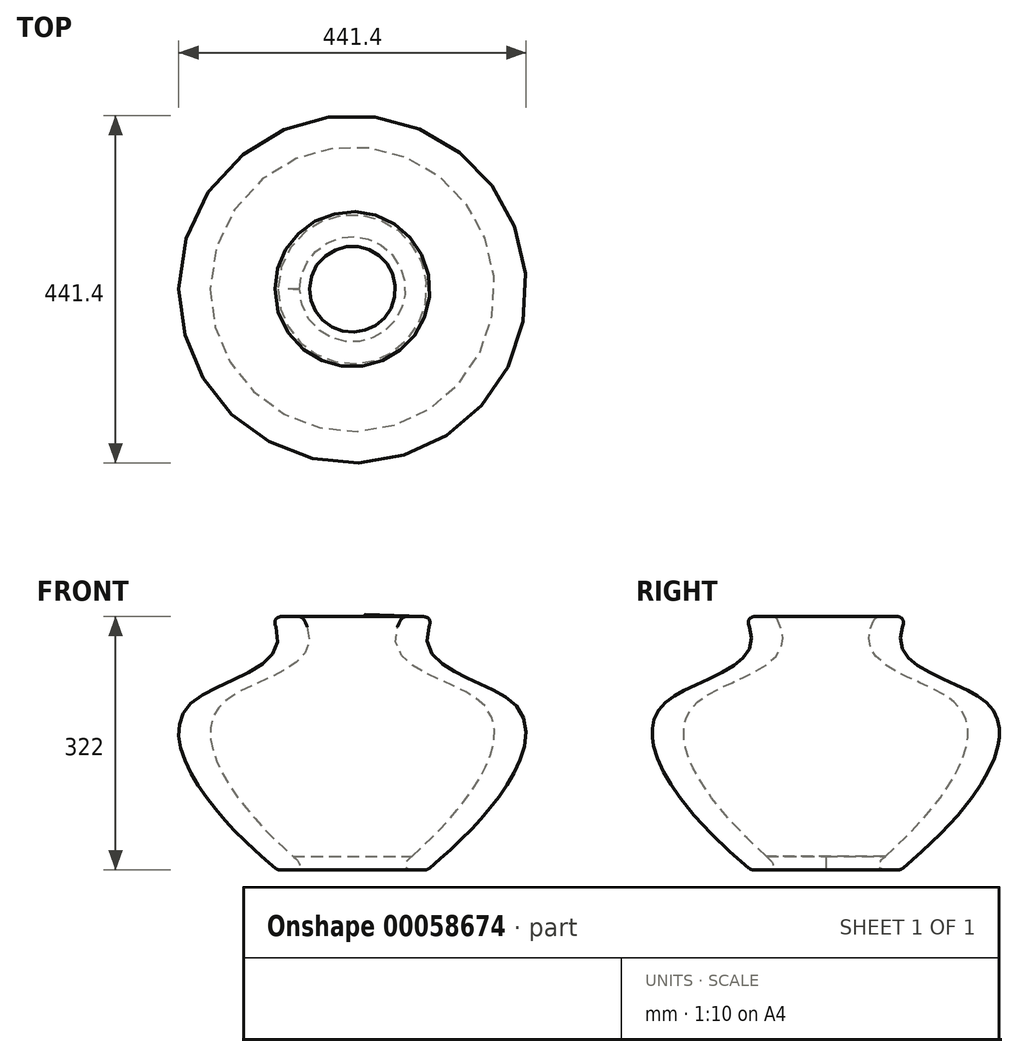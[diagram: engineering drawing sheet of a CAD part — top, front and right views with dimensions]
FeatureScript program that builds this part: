
annotation { "Feature Type Name" : "Feature", "Feature Type Description" : "" }
export const myFeature = defineFeature(function(context is Context, id is Id, definition is map)
    precondition{}
    {
        {
            var Q0;
            Q0=qCreatedBy(makeId("Front.planeOp"),FACE);
            var sketch = newSketch(context, id + "F0", { "sketchPlane" : qUnion([Q0])});
            skFitSpline(sketch, "E0", {"points": [v(-103.82, 122.7) * mm, v(-201.38, 15.63) * mm, v(-198.62, -87.65) * mm, v(-95, -199.3) * mm], "startDerivative": vector(344.72, -563.96) * mm, "endDerivative": vector(293.07, -243.26) * mm});
            skFitSpline(sketch, "E1", {"points": [v(-63.82, 122.7) * mm, v(-161.38, 15.63) * mm, v(-158.62, -87.65) * mm, v(-55, -199.3) * mm], "startDerivative": vector(344.72, -563.96) * mm, "endDerivative": vector(293.07, -243.26) * mm});
            skLineSegment(sketch, "E2", {"start": v(0, 0) * mm, "end": v(0, 73.7) * mm, "construction": true});
            skLineSegment(sketch, "E3", {"start": v(0, 73.7) * mm, "end": v(-15, 73.7) * mm, "construction": true});
            skLineSegment(sketch, "E4", {"start": v(-15, 73.7) * mm, "end": v(-15, 40.7) * mm, "construction": true});
            skLineSegment(sketch, "E5", {"start": v(-15, 40.7) * mm, "end": v(0, 40.7) * mm, "construction": true});
            skLineSegment(sketch, "E6", {"start": v(-25, 73.7) * mm, "end": v(-25, 40.7) * mm, "construction": true});
            skLineSegment(sketch, "E7", {"start": v(-103.82, 122.7) * mm, "end": v(-63.82, 122.7) * mm});
            skLineSegment(sketch, "E8", {"start": v(-95, -199.3) * mm, "end": v(-55, -199.3) * mm});
            skPoint(sketch, "E9", {"position": v(-25, 57.2) * mm});
            skFitSpline(sketch, "E10", {"points": [v(266.45, 104.72) * mm, v(195.35, -10.04) * mm, v(318.2, -171.15) * mm], "startDerivative": vector(-213.61, -240.55) * mm, "endDerivative": vector(297.87, -308.63) * mm});
            skSolve(sketch);
        }
        {
            var Q0;
            Q0=makeQuery(id+"F0.imprint","IMPRINT",FACE,{"disambiguationData":[TD([[makeQuery(id+"F0.imprint","IMPRINT",EDGE,{"derivedFrom":sQuery(id+"F0.wireOp",EDGE,"E0")}),1.0]])]});
            var Q1;
            Q1=sQuery(id+"F0.wireOp",EDGE,"E2");
            revolve(context, id + "F1", {"entities" : qUnion([Q0]), "axis" : qUnion([Q1]), "revolveType" : RevolveType.FULL});
        }
        {
            var Q0;
            Q0=makeQuery(id+"F1.opRevolve","SWEPT_FACE",FACE,{"disambiguationData":[OSD([sQuery(id+"F0.wireOp",EDGE,"E8")])]});
            var Q1;
            Q1=makeQuery(id+"F1.opRevolve","SWEPT_FACE",FACE,{"disambiguationData":[OSD([sQuery(id+"F0.wireOp",EDGE,"E7")])]});
            fillet(context, id + "F2", {"entities" : qUnion([Q0, Q1]), "radius" : 10 * mm, "tangentPropagation" : true, "rho" : 0.5, "crossSection" : FilletCrossSection.CONIC, "allowEdgeOverflow" : false});
        }
    });
